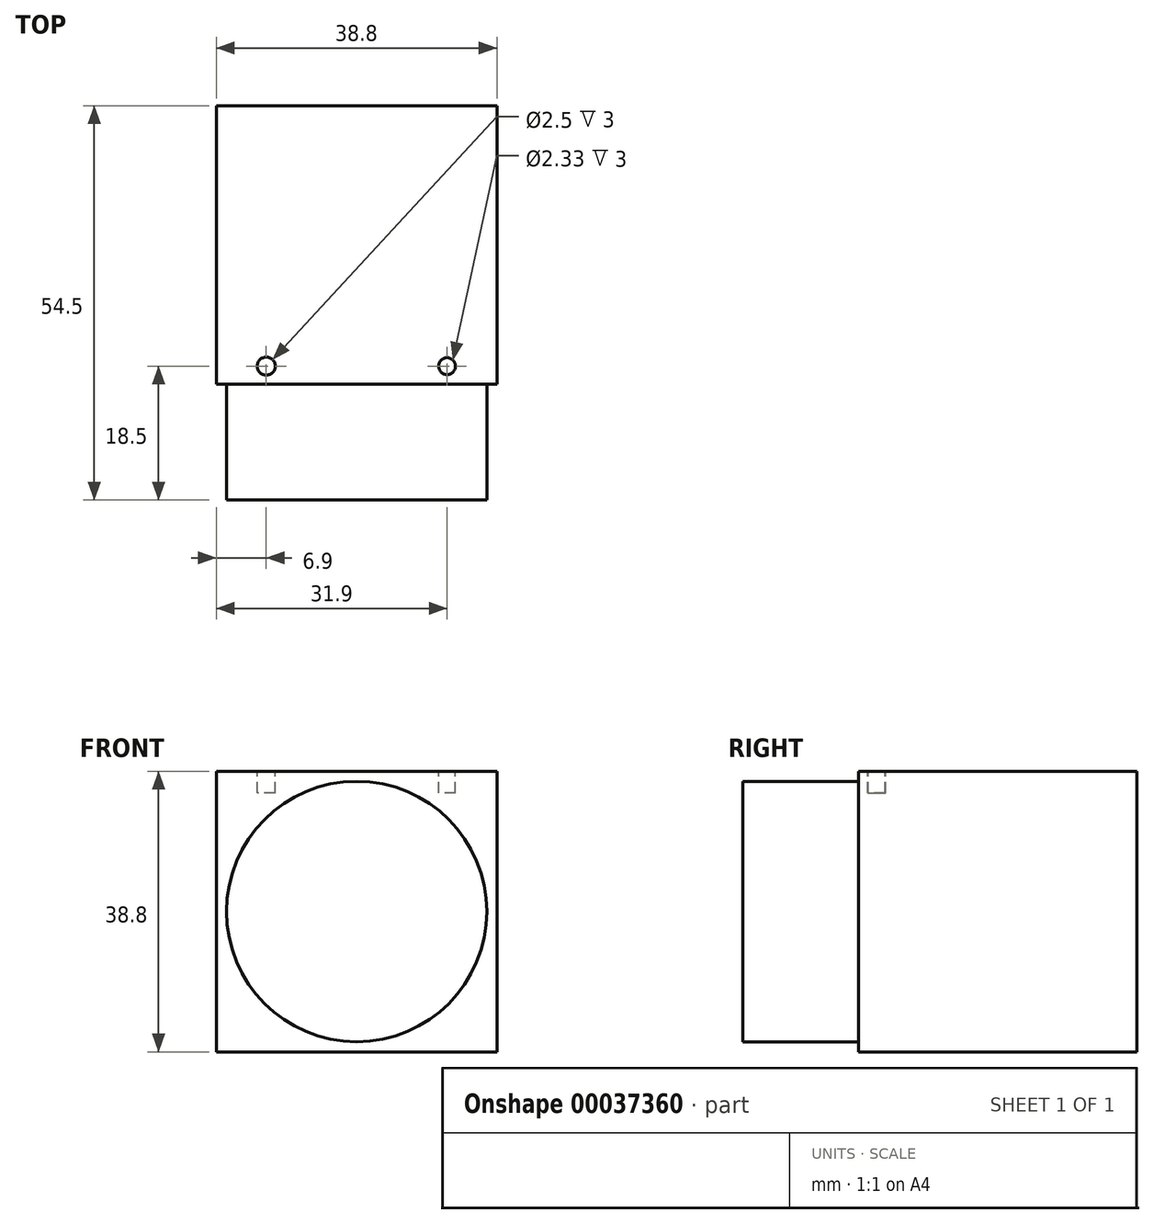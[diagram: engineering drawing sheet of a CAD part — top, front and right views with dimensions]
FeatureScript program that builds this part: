
annotation { "Feature Type Name" : "Feature", "Feature Type Description" : "" }
export const myFeature = defineFeature(function(context is Context, id is Id, definition is map)
    precondition{}
    {
        {
            var Q0;
            Q0=qCreatedBy(makeId("Front.planeOp"),FACE);
            var sketch = newSketch(context, id + "F0", { "sketchPlane" : qUnion([Q0])});
            skLineSegment(sketch, "E0.rect.bottom", {"start": v(19.4, 19.4) * mm, "end": v(-19.4, 19.4) * mm});
            skLineSegment(sketch, "E0.rect.top", {"start": v(19.4, -19.4) * mm, "end": v(-19.4, -19.4) * mm});
            skLineSegment(sketch, "E0.rect.left", {"start": v(19.4, 19.4) * mm, "end": v(19.4, -19.4) * mm});
            skLineSegment(sketch, "E0.rect.right", {"start": v(-19.4, 19.4) * mm, "end": v(-19.4, -19.4) * mm});
            skPoint(sketch, "E0.rect.middle", {"position": v(0, 0) * mm});
            skCircle(sketch, "E1", {"center": v(0, 0) * mm, "radius": 18 * mm});
            skSolve(sketch);
        }
        {
            var Q0;
            Q0=makeQuery(id+"F0.imprint","IMPRINT",FACE,{"disambiguationData":[TD([[makeQuery(id+"F0.imprint","IMPRINT",EDGE,{"derivedFrom":sQuery(id+"F0.wireOp",EDGE,"E0.rect.bottom")}),1.0]])]});
            var Q1;
            Q1=makeQuery(id+"F0.imprint","IMPRINT",FACE,{"disambiguationData":[TD([[makeQuery(id+"F0.imprint","IMPRINT",EDGE,{"derivedFrom":sQuery(id+"F0.wireOp",EDGE,"E1")}),1.0]])]});
            extrude(context, id + "F1", {"entities" : qUnion([Q0, Q1]), "oppositeDirection" : true, "depth" : 38.5 * mm});
        }
        {
            var Q0;
            Q0=makeQuery(id+"F0.imprint","IMPRINT",FACE,{"disambiguationData":[TD([[makeQuery(id+"F0.imprint","IMPRINT",EDGE,{"derivedFrom":sQuery(id+"F0.wireOp",EDGE,"E1")}),1.0]])]});
            extrude(context, id + "F2", {"entities" : qUnion([Q0]), "operationType" : NewBodyOperationType.ADD, "depth" : 16 * mm});
        }
        {
            var Q0;
            Q0=makeQuery(id+"F1.opExtrude","SWEPT_FACE",FACE,{"disambiguationData":[OSD([sQuery(id+"F0.wireOp",EDGE,"E0.rect.bottom")])]});
            var sketch = newSketch(context, id + "F3", { "sketchPlane" : qUnion([Q0])});
            skCircle(sketch, "E2", {"center": v(-12.5, 2.5) * mm, "radius": 1.25 * mm});
            skCircle(sketch, "E3", {"center": v(12.5, 2.5) * mm, "radius": 1.16 * mm});
            skLineSegment(sketch, "E4", {"start": v(-12.5, 2.5) * mm, "end": v(12.5, 2.5) * mm, "construction": true});
            skPoint(sketch, "E5", {"position": v(0, 2.5) * mm});
            skSolve(sketch);
        }
        {
            var Q0;
            Q0=makeQuery(id+"F3.imprint","IMPRINT",FACE,{"disambiguationData":[TD([[makeQuery(id+"F3.imprint","IMPRINT",EDGE,{"derivedFrom":sQuery(id+"F3.wireOp",EDGE,"E3")}),1.0]])]});
            var Q1;
            Q1=makeQuery(id+"F3.imprint","IMPRINT",FACE,{"disambiguationData":[TD([[makeQuery(id+"F3.imprint","IMPRINT",EDGE,{"derivedFrom":sQuery(id+"F3.wireOp",EDGE,"E2")}),1.0]])]});
            var Q2;
            Q2=sQuery(id+"F3.wireOp",EDGE,"E2");
            var Q3;
            Q3=sQuery(id+"F3.wireOp",EDGE,"E3");
            extrude(context, id + "F4", {"entities" : qUnion([Q0, Q1]), "operationType" : NewBodyOperationType.REMOVE, "surfaceEntities" : qUnion([Q2, Q3]), "oppositeDirection" : true, "depth" : 3 * mm});
        }
    });
